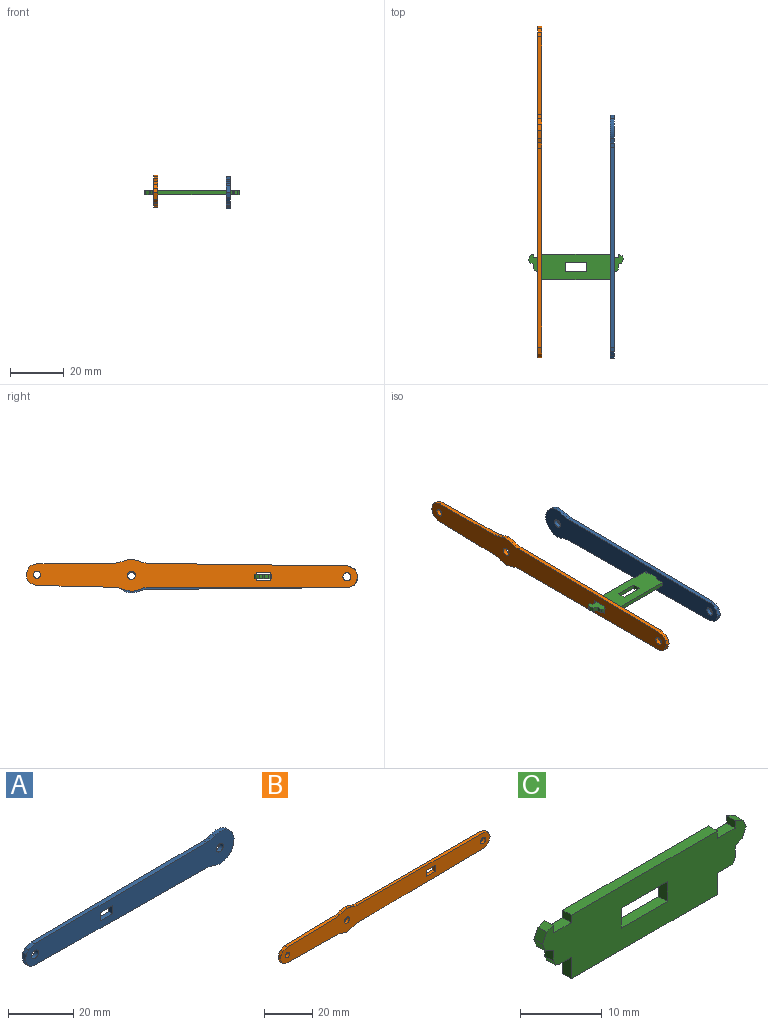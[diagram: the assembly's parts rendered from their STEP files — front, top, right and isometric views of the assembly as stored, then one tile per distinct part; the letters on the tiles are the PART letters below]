
ASSEMBLY  parts=3 mates=2
PART A: 23 faces, bbox 90.1x1.5x12 mm
  f0: plane 1.84x1.5mm, normal (-0.3,0,-0.95), area 2.9mm2, adj f1,f17,f20,f21
  f1: cylinder r=6mm len=7.21mm, axis (0,1,0), area 12mm2, adj f0,f2,f20,f21
  f2: cylinder r=6mm len=7.42mm, axis (0,1,0), area 12mm2, adj f1,f3,f20,f21
  f3: cylinder r=6mm len=7.21mm, axis (0,1,0), area 12mm2, adj f2,f4,f20,f21
  f4: plane 1.5x1.43mm, normal (-0.32,0,0.95), area 2.3mm2, adj f3,f5,f20,f21
  f5: plane 1.92x1.5mm, normal (-0.12,0,0.99), area 2.9mm2, adj f4,f6,f20,f21
  f6: plane 74.29x1.5mm, normal (-0.01,0,1), area 111.4mm2, adj f5,f7,f20,f21
  f7: plane 2.53x1.5mm, normal (-0.35,0,0.94), area 4.1mm2, adj f6,f8,f20,f21
  f8: plane 1.5x1.35mm, normal (-0.79,0,0.61), area 2.6mm2, adj f7,f9,f20,f21
  f9: plane 1.72x1.5mm, normal (-0.98,0,0.22), area 2.6mm2, adj f8,f10,f20,f21
  f10: plane 2.54x1.5mm, normal (-0.94,0,-0.34), area 4.1mm2, adj f9,f11,f20,f21
  f11: plane 1.5x1.34mm, normal (-0.62,0,-0.78), area 2.6mm2, adj f10,f12,f20,f21
  f12: plane 1.71x1.5mm, normal (-0.23,0,-0.97), area 2.6mm2, adj f11,f13,f20,f21
  f13: plane 74.29x1.5mm, normal (-0.01,0,-1), area 111.4mm2, adj f12,f17,f20,f21
  f14: plane 3.1x1.5mm, normal (1,0,0), area 4.6mm2, adj f15,f18,f20,f21
  f15: plane 5.37x1.5mm, normal (0,0,-1), area 8.1mm2, adj f14,f16,f20,f21
  f16: plane 3.1x1.5mm, normal (-1,0,0), area 4.6mm2, adj f15,f18,f20,f21
  f17: plane 1.51x1.5mm, normal (-0.1,0,-1), area 2.3mm2, adj f0,f13,f20,f21
  f18: plane 5.37x1.5mm, normal (0,0,1), area 8.1mm2, adj f14,f16,f20,f21
  f19: cylinder r=1.5mm len=3mm, axis (0,1,0), area 14.1mm2, adj f20,f21
  f20: plane 90.1x12mm, normal (0,-1,0), area 760.4mm2, adj f0,f1,f2,f3,f4,f5,f6,f7
  f21: plane 90.1x12mm, normal (0,1,0), area 760.4mm2, adj f0,f1,f2,f3,f4,f5,f6,f7
  f22: cylinder r=1.5mm len=3mm, axis (0,-1,0), area 14.1mm2, adj f20,f21
PART B: 41 faces, bbox 123.1x1.5x12 mm
  f0: plane 3.1x1.5mm, normal (-1,0,0), area 4.6mm2, adj f1,f35,f39,f40
  f1: plane 5.37x1.5mm, normal (0,0,1), area 8.1mm2, adj f0,f2,f39,f40
  f2: plane 3.1x1.5mm, normal (1,0,0), area 4.6mm2, adj f1,f35,f39,f40
  f3: plane 1.71x1.5mm, normal (-0.23,0,-0.97), area 2.6mm2, adj f4,f36,f39,f40
  f4: plane 1.5x0.1mm, normal (0,0,-1), area 0.2mm2, adj f3,f5,f39,f40
  f5: plane 28.82x1.5mm, normal (-0.01,0,-1), area 43.2mm2, adj f4,f6,f39,f40
  f6: plane 1.6x1.5mm, normal (-0.11,0,-0.99), area 2.4mm2, adj f5,f7,f39,f40
  f7: plane 1.93x1.5mm, normal (-0.33,0,-0.94), area 3.1mm2, adj f6,f8,f39,f40
  f8: plane 1.5x0.06mm, normal (-0.16,0,-0.99), area 0.1mm2, adj f7,f9,f39,f40
  f9: plane 2.39x1.5mm, normal (-0.27,0,-0.96), area 3.7mm2, adj f8,f10,f39,f40
  f10: plane 3.06x1.5mm, normal (0.2,0,-0.98), area 4.7mm2, adj f9,f11,f39,f40
  f11: plane 1.5x0.06mm, normal (0.74,0,0.67), area 0.1mm2, adj f10,f12,f39,f40
  f12: plane 1.51x1.5mm, normal (0.37,0,-0.93), area 2.4mm2, adj f11,f13,f39,f40
  f13: plane 2.05x1.5mm, normal (0.14,0,-0.99), area 3.1mm2, adj f12,f14,f39,f40
  f14: plane 73.74x1.5mm, normal (0.01,0,-1), area 110.6mm2, adj f13,f15,f39,f40
  f15: plane 2.54x1.5mm, normal (0.35,0,-0.94), area 4.1mm2, adj f14,f16,f39,f40
  f16: plane 1.5x1.35mm, normal (0.79,0,-0.61), area 2.6mm2, adj f15,f17,f39,f40
  f17: plane 1.72x1.5mm, normal (0.98,0,-0.21), area 2.6mm2, adj f16,f18,f39,f40
  f18: plane 2.54x1.5mm, normal (0.94,0,0.34), area 4.1mm2, adj f17,f19,f39,f40
  f19: plane 1.5x1.35mm, normal (0.61,0,0.79), area 2.6mm2, adj f18,f20,f39,f40
  f20: plane 1.72x1.5mm, normal (0.22,0,0.98), area 2.6mm2, adj f19,f21,f39,f40
  f21: plane 73.75x1.5mm, normal (0,0,1), area 110.6mm2, adj f20,f22,f39,f40
  f22: plane 1.62x1.5mm, normal (0.1,0,0.99), area 2.4mm2, adj f21,f23,f39,f40
  f23: plane 1.95x1.5mm, normal (0.33,0,0.94), area 3.1mm2, adj f22,f24,f39,f40
  f24: plane 2.39x1.5mm, normal (0.25,0,0.97), area 3.7mm2, adj f23,f25,f39,f40
  f25: plane 3.06x1.5mm, normal (-0.21,0,0.98), area 4.7mm2, adj f24,f26,f39,f40
  f26: plane 1.5x1.49mm, normal (-0.37,0,0.93), area 2.4mm2, adj f25,f27,f39,f40
  f27: plane 2.02x1.5mm, normal (-0.15,0,0.99), area 3.1mm2, adj f26,f28,f39,f40
  f28: plane 28.81x1.5mm, normal (-0.02,0,1), area 43.2mm2, adj f27,f29,f39,f40
  f29: plane 1.5x0.1mm, normal (0,0,1), area 0.2mm2, adj f28,f30,f39,f40
  f30: plane 2.51x1.5mm, normal (-0.36,0,0.93), area 4mm2, adj f29,f31,f39,f40
  f31: plane 1.5x1.35mm, normal (-0.8,0,0.6), area 2.5mm2, adj f30,f32,f39,f40
  f32: plane 1.71x1.5mm, normal (-0.98,0,0.21), area 2.6mm2, adj f31,f33,f39,f40
  f33: plane 2.53x1.5mm, normal (-0.94,0,-0.34), area 4mm2, adj f32,f36,f39,f40
  f34: cylinder r=1.5mm len=3mm, axis (0,1,0), area 14.1mm2, adj f39,f40
  f35: plane 5.37x1.5mm, normal (0,0,-1), area 8.1mm2, adj f0,f2,f39,f40
  f36: plane 1.5x1.33mm, normal (-0.62,0,-0.79), area 2.5mm2, adj f3,f33,f39,f40
  f37: cylinder r=1.5mm len=3mm, axis (0,1,0), area 14.1mm2, adj f39,f40
  f38: cylinder r=1.32mm len=2.65mm, axis (0,1,0), area 12.5mm2, adj f39,f40
  f39: plane 123.1x12.02mm, normal (0,-1,0), area 1011mm2, adj f0,f1,f2,f3,f4,f5,f6,f7
  f40: plane 123.1x12.02mm, normal (0,1,0), area 1011mm2, adj f0,f1,f2,f3,f4,f5,f6,f7
PART C: 32 faces, bbox 35.3x1.5x9.5 mm
  f0: plane 3x1.5mm, normal (1,0,0), area 4.5mm2, adj f1,f29,f30,f31
  f1: plane 8x1.5mm, normal (0,0,-1), area 12mm2, adj f0,f2,f30,f31
  f2: plane 3x1.5mm, normal (-1,0,0), area 4.5mm2, adj f1,f29,f30,f31
  f3: plane 1.5x1.18mm, normal (0.36,0,-0.93), area 1.9mm2, adj f4,f28,f30,f31
  f4: plane 1.5x1.42mm, normal (0.9,0,-0.44), area 2.4mm2, adj f3,f5,f30,f31
  f5: plane 1.5x1.25mm, normal (0.93,0,0.38), area 2mm2, adj f4,f6,f30,f31
  f6: plane 1.5x1.37mm, normal (0.42,0,0.91), area 2.3mm2, adj f5,f7,f30,f31
  f7: plane 1.5x1.12mm, normal (-1,0,0), area 1.7mm2, adj f6,f8,f30,f31
  f8: plane 3.1x1.5mm, normal (0,0,1), area 4.6mm2, adj f7,f9,f30,f31
  f9: plane 1.5x1.13mm, normal (1,0,0), area 1.7mm2, adj f8,f10,f30,f31
  f10: plane 25.3x1.5mm, normal (0,0,1), area 38mm2, adj f9,f11,f30,f31
  f11: plane 1.5x1.13mm, normal (-1,0,0), area 1.7mm2, adj f10,f12,f30,f31
  f12: plane 3.1x1.5mm, normal (0,0,1), area 4.6mm2, adj f11,f13,f30,f31
  f13: plane 1.5x1.11mm, normal (1,0,0), area 1.7mm2, adj f12,f14,f30,f31
  f14: plane 1.5x1.18mm, normal (-0.32,0,0.95), area 1.9mm2, adj f13,f15,f30,f31
  f15: plane 1.5x1.47mm, normal (-0.9,0,0.43), area 2.4mm2, adj f14,f16,f30,f31
  f16: plane 1.5x1.24mm, normal (-0.94,0,-0.34), area 2mm2, adj f15,f17,f30,f31
  f17: plane 1.5x1.43mm, normal (-0.41,0,-0.91), area 2.4mm2, adj f16,f18,f30,f31
  f18: plane 1.6x1.5mm, normal (-1,0,0), area 2.4mm2, adj f17,f19,f30,f31
  f19: plane 1.5x0.74mm, normal (-0.92,0,-0.39), area 1.2mm2, adj f18,f20,f30,f31
  f20: plane 1.5x0.79mm, normal (-0.29,0,-0.96), area 1.2mm2, adj f19,f21,f30,f31
  f21: plane 2x1.5mm, normal (0,0,-1), area 3mm2, adj f20,f22,f30,f31
  f22: plane 3.21x1.5mm, normal (-1,0,0), area 4.8mm2, adj f21,f23,f30,f31
  f23: plane 25.3x1.5mm, normal (0,0,-1), area 38mm2, adj f22,f24,f30,f31
  f24: plane 3.21x1.5mm, normal (1,0,0), area 4.8mm2, adj f23,f25,f30,f31
  f25: plane 2.31x1.5mm, normal (0,0,-1), area 3.5mm2, adj f24,f26,f30,f31
  f26: plane 1.5x0.49mm, normal (0.29,0,-0.96), area 0.8mm2, adj f25,f27,f30,f31
  f27: plane 1.5x0.63mm, normal (0.9,0,-0.44), area 1mm2, adj f26,f28,f30,f31
  f28: plane 1.8x1.5mm, normal (1,0,0), area 2.7mm2, adj f3,f27,f30,f31
  f29: plane 8x1.5mm, normal (0,0,1), area 12mm2, adj f0,f2,f30,f31
  f30: plane 35.25x9.54mm, normal (0,-1,0), area 259mm2, adj f0,f1,f2,f3,f4,f5,f6,f7
  f31: plane 35.25x9.54mm, normal (0,1,0), area 259mm2, adj f0,f1,f2,f3,f4,f5,f6,f7
PLACE A rot(axis=(-0.71,-0.71,0),180deg) t=(14.15,60.52,77.68)mm
PLACE B rot(axis=(-0.71,0.71,0),180deg) t=(-14.15,-36.83,89.38)mm
PLACE C rot(axis=(-1,0,0),90deg) t=(19.63,-42.58,0)mm
MATE fastened A.f22 <-> B.f34  axis (-1,0,0) through (12.65,-29.91,0.75)mm
MATE fastened A.f20 <-> C.f24  axis (-1,0,0) through (12.65,-1.81,0.75)mm
